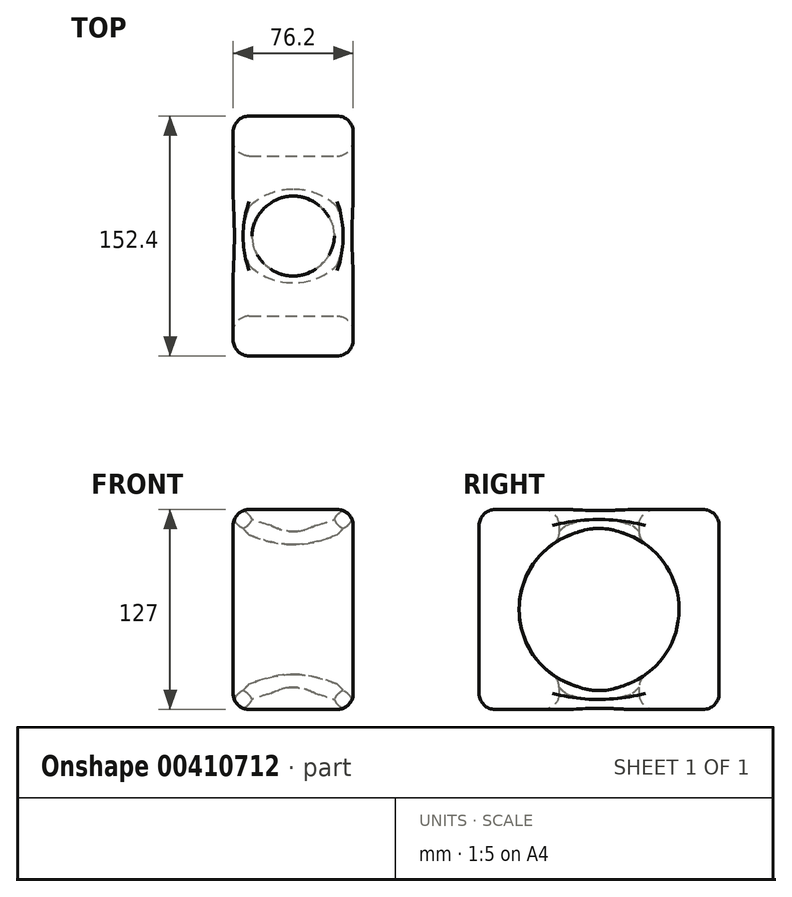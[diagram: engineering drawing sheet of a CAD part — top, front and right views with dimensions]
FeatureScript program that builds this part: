
annotation { "Feature Type Name" : "Feature", "Feature Type Description" : "" }
export const myFeature = defineFeature(function(context is Context, id is Id, definition is map)
    precondition{}
    {
        {
            var Q0;
            Q0=qCreatedBy(makeId("Top.planeOp"),FACE);
            var sketch = newSketch(context, id + "F0", { "sketchPlane" : qUnion([Q0])});
            skLineSegment(sketch, "E0.bottom", {"start": v(0, 0) * mm, "end": v(76.2, 0) * mm});
            skLineSegment(sketch, "E0.top", {"start": v(0, 127) * mm, "end": v(76.2, 127) * mm});
            skLineSegment(sketch, "E0.left", {"start": v(0, 0) * mm, "end": v(0, 127) * mm});
            skLineSegment(sketch, "E0.right", {"start": v(76.2, 0) * mm, "end": v(76.2, 127) * mm});
            skSolve(sketch);
        }
        {
            var Q0;
            Q0=makeQuery(id+"F0.imprint","IMPRINT",FACE,{"disambiguationData":[TD([[makeQuery(id+"F0.imprint","IMPRINT",EDGE,{"derivedFrom":sQuery(id+"F0.wireOp",EDGE,"E0.bottom")}),1.0]])]});
            extrude(context, id + "F1", {"entities" : qUnion([Q0]), "depth" : 152.4 * mm});
        }
        {
            var Q0;
            Q0=makeQuery(id+"F1.opExtrude","SWEPT_FACE",FACE,{"disambiguationData":[OSD([sQuery(id+"F0.wireOp",EDGE,"E0.top")])]});
            var sketch = newSketch(context, id + "F2", { "sketchPlane" : qUnion([Q0])});
            skCircle(sketch, "E1", {"center": v(-38.1, 76.2) * mm, "radius": 25.4 * mm});
            skSolve(sketch);
        }
        {
            var Q0;
            Q0=makeQuery(id+"F2.imprint","IMPRINT",FACE,{"disambiguationData":[TD([[makeQuery(id+"F2.imprint","IMPRINT",EDGE,{"derivedFrom":sQuery(id+"F2.wireOp",EDGE,"E1")}),1.0]])]});
            extrude(context, id + "F3", {"entities" : qUnion([Q0]), "operationType" : NewBodyOperationType.REMOVE, "endBound" : BoundingType.UP_TO_NEXT, "oppositeDirection" : true, "depth" : 191.52 * mm});
        }
        {
            var Q0;
            Q0=makeQuery(id+"F1.opExtrude","SWEPT_FACE",FACE,{"disambiguationData":[OSD([sQuery(id+"F0.wireOp",EDGE,"E0.right")])]});
            var sketch = newSketch(context, id + "F4", { "sketchPlane" : qUnion([Q0])});
            skCircle(sketch, "E2", {"center": v(63.5, 76.2) * mm, "radius": 50.8 * mm});
            skSolve(sketch);
        }
        {
            var Q0;
            Q0 = qSketchRegion(id + "F4", true);
            extrude(context, id + "F5", {"entities" : qUnion([Q0]), "operationType" : NewBodyOperationType.REMOVE, "endBound" : BoundingType.THROUGH_ALL, "oppositeDirection" : true, "depth" : 25.4 * mm});
        }
        {
            var Q0;
            Q0=makeQuery(id+"F1.opExtrude","SWEPT_FACE",FACE,{"disambiguationData":[OSD([sQuery(id+"F0.wireOp",EDGE,"E0.top")])]});
            var Q1;
            Q1=makeQuery(id+"F3.boolean.opBoolean","COPY",FACE,{"derivedFrom":makeQuery(id+"F3.opExtrude","SWEPT_FACE",FACE,{"disambiguationData":[OSD([sQuery(id+"F2.wireOp",EDGE,"E1")])]})});
            var Q2;
            Q2=makeQuery(id+"F1.opExtrude","SWEPT_FACE",FACE,{"disambiguationData":[OSD([sQuery(id+"F0.wireOp",EDGE,"E0.left")])]});
            var Q3;
            Q3=makeQuery(id+"F1.opExtrude","CAP_FACE",FACE,{"disambiguationData":[OSD([sQuery(id+"F0.wireOp",EDGE,"E0.bottom"),sQuery(id+"F0.wireOp",EDGE,"E0.top"),sQuery(id+"F0.wireOp",EDGE,"E0.left"),sQuery(id+"F0.wireOp",EDGE,"E0.right")])],"isStart":false});
            var Q4;
            Q4=makeQuery(id+"F1.opExtrude","SWEPT_EDGE",EDGE,{"disambiguationData":[OSD([sQuery(id+"F0.wireOp",EDGE,"E0.bottom"),sQuery(id+"F0.wireOp",EDGE,"E0.right")])]});
            var Q5;
            Q5=makeQuery(id+"F1.opExtrude","CAP_EDGE",EDGE,{"disambiguationData":[OSD([sQuery(id+"F0.wireOp",EDGE,"E0.bottom")])],"isStart":true});
            var Q6;
            Q6=makeQuery(id+"F1.opExtrude","SWEPT_FACE",FACE,{"disambiguationData":[OSD([sQuery(id+"F0.wireOp",EDGE,"E0.right")])]});
            fillet(context, id + "F6", {"entities" : qUnion([Q0, Q1, Q2, Q3, Q4, Q5, Q6]), "radius" : 10.16 * mm, "tangentPropagation" : true, "allowEdgeOverflow" : false});
        }
        {
            var Q0;
            Q0=makeQuery(id+"F1.opExtrude","SWEPT_BODY",BODY,{"disambiguationData":[OSD([sQuery(id+"F0.wireOp",EDGE,"E0.bottom"),sQuery(id+"F0.wireOp",EDGE,"E0.top"),sQuery(id+"F0.wireOp",EDGE,"E0.left"),sQuery(id+"F0.wireOp",EDGE,"E0.right")])]});
            var Q1;
            {var subQ0=sQuery(id+"F0.wireOp",EDGE,"E0.bottom");Q1=makeQuery(id+"F6.opFillet","BLEND_EDGE",EDGE,{"blendedFrom":[makeQuery(id+"F1.opExtrude","CAP_EDGE",EDGE,{"disambiguationData":[OSD([subQ0])],"isStart":true}),makeQuery(id+"F1.opExtrude","CAP_FACE",FACE,{"disambiguationData":[OSD([subQ0,sQuery(id+"F0.wireOp",EDGE,"E0.top"),sQuery(id+"F0.wireOp",EDGE,"E0.left"),sQuery(id+"F0.wireOp",EDGE,"E0.right")])],"isStart":true})],"blendedInto":[makeQuery(id+"F1.opExtrude","CAP_FACE",FACE,{"disambiguationData":[OSD([subQ0,sQuery(id+"F0.wireOp",EDGE,"E0.top"),sQuery(id+"F0.wireOp",EDGE,"E0.left"),sQuery(id+"F0.wireOp",EDGE,"E0.right")])],"isStart":true})]});}
            transform(context, id + "F7", {"entities" : qUnion([Q0]), "transformType" : TransformType.ROTATION, "transformAxis" : qUnion([Q1]), "angle" : 90 * degree, "oppositeDirection" : true, "makeCopy" : false});
        }
        {
            var Q0;
            Q0=makeQuery(id+"F1.opExtrude","SWEPT_BODY",BODY,{"disambiguationData":[OSD([sQuery(id+"F0.wireOp",EDGE,"E0.bottom"),sQuery(id+"F0.wireOp",EDGE,"E0.top"),sQuery(id+"F0.wireOp",EDGE,"E0.left"),sQuery(id+"F0.wireOp",EDGE,"E0.right")])]});
            var Q1;
            {var subQ0=sQuery(id+"F0.wireOp",EDGE,"E0.left");var subQ1=sQuery(id+"F0.wireOp",EDGE,"E0.bottom");Q1=makeQuery(id+"F6.opFillet","BLEND_VERTEX",VERTEX,{"blendedFrom":[makeQuery(id+"F1.opExtrude","CAP_VERTEX",VERTEX,{"disambiguationData":[OSD([subQ1,subQ0])],"isStart":true}),makeQuery(id+"F1.opExtrude","CAP_EDGE",EDGE,{"disambiguationData":[OSD([subQ1])],"isStart":true}),makeQuery(id+"F1.opExtrude","CAP_EDGE",EDGE,{"disambiguationData":[OSD([subQ0])],"isStart":true}),makeQuery(id+"F1.opExtrude","CAP_FACE",FACE,{"disambiguationData":[OSD([subQ1,sQuery(id+"F0.wireOp",EDGE,"E0.top"),subQ0,sQuery(id+"F0.wireOp",EDGE,"E0.right")])],"isStart":true})],"blendedInto":[makeQuery(id+"F1.opExtrude","CAP_FACE",FACE,{"disambiguationData":[OSD([subQ1,sQuery(id+"F0.wireOp",EDGE,"E0.top"),subQ0,sQuery(id+"F0.wireOp",EDGE,"E0.right")])],"isStart":true})]});}
            var Q2;
            Q2=qCreatedBy(makeId("Origin.pointOp"),VERTEX);
            transform(context, id + "F8", {"entities" : qUnion([Q0]), "transformType" : TransformType.TRANSLATION_ENTITY, "oppositeDirectionEntity" : false, "transformLine" : qUnion([Q1, Q2]), "makeCopy" : false});
        }
    });
